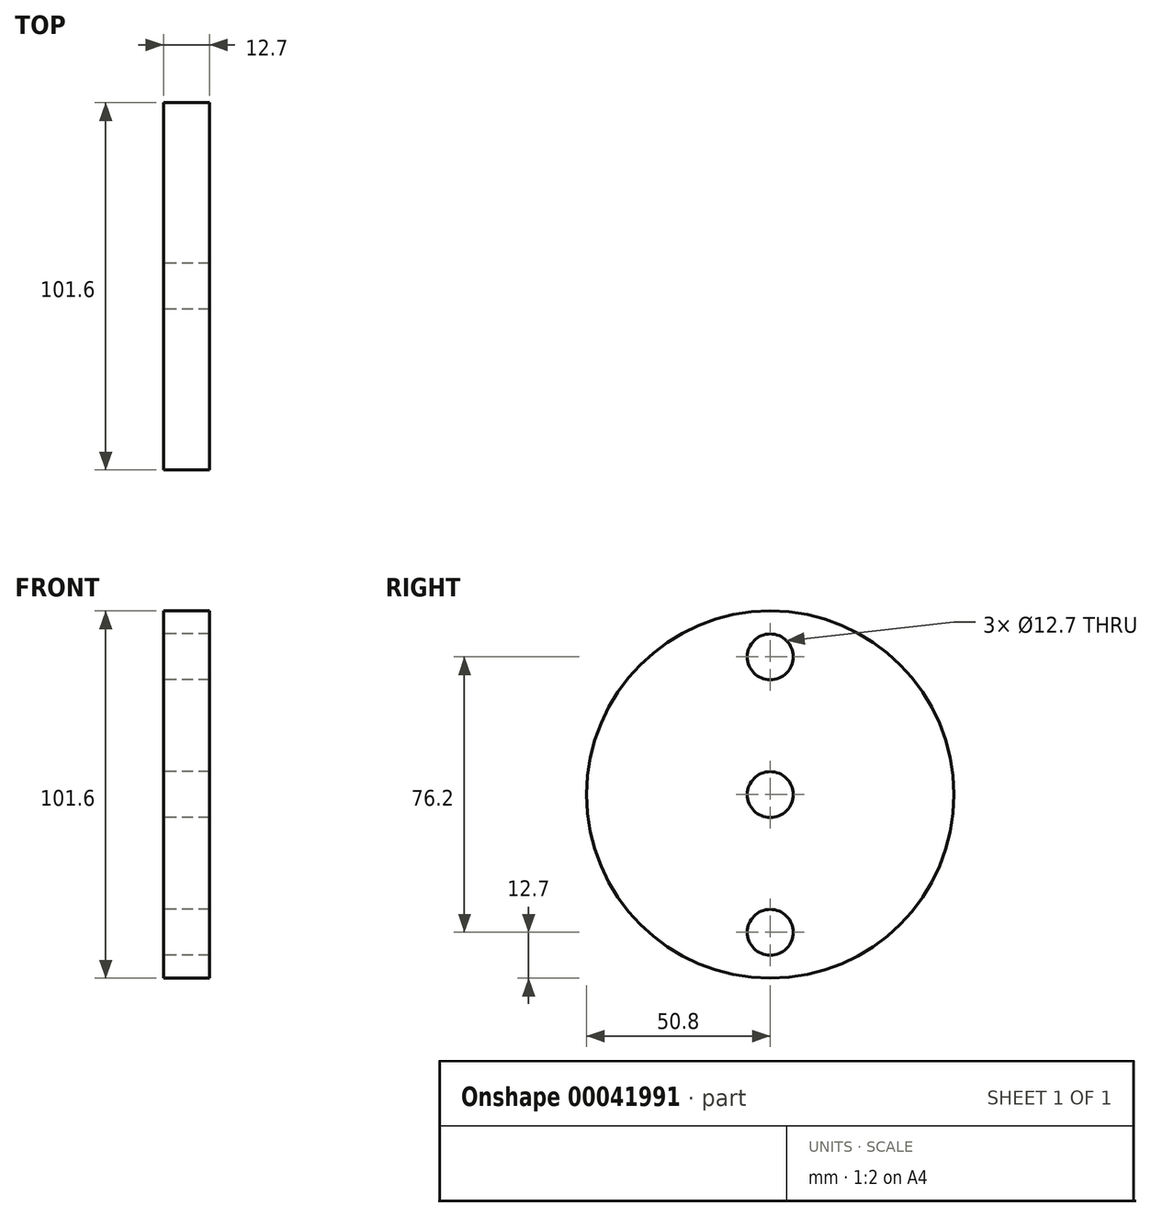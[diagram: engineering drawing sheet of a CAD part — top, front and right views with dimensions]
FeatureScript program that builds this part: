
annotation { "Feature Type Name" : "Feature", "Feature Type Description" : "" }
export const myFeature = defineFeature(function(context is Context, id is Id, definition is map)
    precondition{}
    {
        {
            var Q0;
            Q0=qCreatedBy(makeId("Right.planeOp"),FACE);
            var sketch = newSketch(context, id + "F0", { "sketchPlane" : qUnion([Q0])});
            skLineSegment(sketch, "E0", {"start": v(0, 0) * mm, "end": v(0, 38.1) * mm});
            skCircle(sketch, "E1", {"center": v(0, 38.1) * mm, "radius": 6.35 * mm});
            skCircle(sketch, "E2", {"center": v(0, 0) * mm, "radius": 6.35 * mm});
            skCircle(sketch, "E3", {"center": v(0, 38.1) * mm, "radius": 50.8 * mm});
            skCircle(sketch, "E4", {"center": v(0, 76.2) * mm, "radius": 6.35 * mm});
            skSolve(sketch);
        }
        {
            var Q0;
            Q0=makeQuery(id+"F0.imprint","IMPRINT",FACE,{"disambiguationData":[TD([[makeQuery(id+"F0.imprint","IMPRINT",EDGE,{"derivedFrom":sQuery(id+"F0.wireOp",EDGE,"E1")}),-1.0]])]});
            extrude(context, id + "F1", {"entities" : qUnion([Q0]), "depth" : 12.7 * mm});
        }
    });
